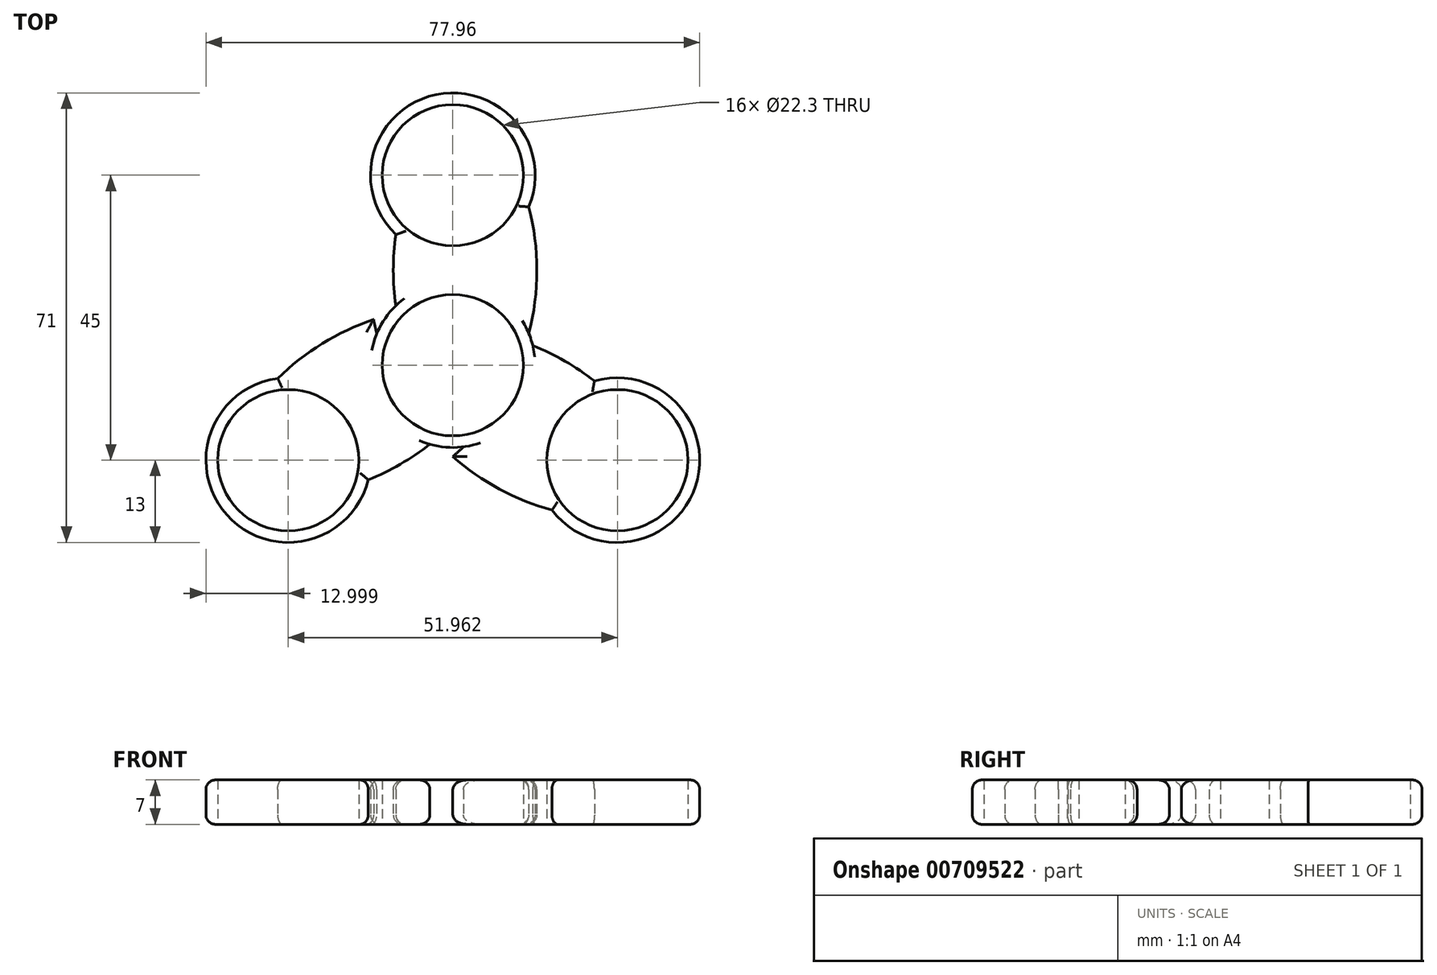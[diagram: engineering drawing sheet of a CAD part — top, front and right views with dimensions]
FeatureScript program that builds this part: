
annotation { "Feature Type Name" : "Feature", "Feature Type Description" : "" }
export const myFeature = defineFeature(function(context is Context, id is Id, definition is map)
    precondition{}
    {
        {
            var Q0;
            Q0=qCreatedBy(makeId("Top.planeOp"),FACE);
            var sketch = newSketch(context, id + "F0", { "sketchPlane" : qUnion([Q0])});
            skCircle(sketch, "E0", {"center": v(0, 0) * mm, "radius": 11.15 * mm});
            skCircle(sketch, "E1", {"center": v(0, 0) * mm, "radius": 13 * mm});
            skCircle(sketch, "E2", {"center": v(0, 30) * mm, "radius": 11.15 * mm});
            skCircle(sketch, "E3", {"center": v(0, 30) * mm, "radius": 13 * mm});
            skArc(sketch, "E4", {"start": v(12, 5) * mm, "mid": v(13.27, 15) * mm, "end": v(12, 25) * mm});
            skArc(sketch, "E5", {"start": v(9, 9.38) * mm, "mid": v(9.4, 15) * mm, "end": v(9, 20.62) * mm});
            skArc(sketch, "E6.MirrorCS", {"start": v(-9, 9.38) * mm, "mid": v(-9.4, 15) * mm, "end": v(-9, 20.62) * mm});
            skArc(sketch, "E7.MirrorCS", {"start": v(-12, 5) * mm, "mid": v(-13.27, 15) * mm, "end": v(-12, 25) * mm});
            skCircle(sketch, "E8.1.0", {"center": v(-25.98, -15) * mm, "radius": 13 * mm});
            skCircle(sketch, "E8.1.1", {"center": v(-25.98, -15) * mm, "radius": 11.15 * mm});
            skArc(sketch, "E8.1.2", {"start": v(1.67, -12.9) * mm, "mid": v(-6.36, -19) * mm, "end": v(-15.65, -22.9) * mm});
            skArc(sketch, "E8.1.5", {"start": v(-3.62, -12.48) * mm, "mid": v(-8.3, -15.64) * mm, "end": v(-13.36, -18.1) * mm});
            skArc(sketch, "E8.1.6", {"start": v(-10.33, 7.9) * mm, "mid": v(-19.63, 4) * mm, "end": v(-27.65, -2.1) * mm});
            skArc(sketch, "E8.1.7", {"start": v(-12.62, 3.1) * mm, "mid": v(-17.69, 0.64) * mm, "end": v(-22.36, -2.52) * mm});
            skCircle(sketch, "E8.2.0", {"center": v(25.98, -15) * mm, "radius": 13 * mm});
            skCircle(sketch, "E8.2.1", {"center": v(25.98, -15) * mm, "radius": 11.15 * mm});
            skArc(sketch, "E8.2.2", {"start": v(10.33, 7.9) * mm, "mid": v(19.63, 4) * mm, "end": v(27.65, -2.1) * mm});
            skArc(sketch, "E8.2.5", {"start": v(12.62, 3.1) * mm, "mid": v(17.69, 0.64) * mm, "end": v(22.36, -2.52) * mm});
            skArc(sketch, "E8.2.6", {"start": v(-1.67, -12.9) * mm, "mid": v(6.36, -19) * mm, "end": v(15.65, -22.9) * mm});
            skArc(sketch, "E8.2.7", {"start": v(3.62, -12.48) * mm, "mid": v(8.3, -15.64) * mm, "end": v(13.36, -18.1) * mm});
            skSolve(sketch);
        }
        {
            var Q0;
            Q0=makeQuery(id+"F0.imprint","IMPRINT",FACE,{"disambiguationData":[TD([[makeQuery(id+"F0.imprint","IMPRINT",EDGE,{"derivedFrom":sQuery(id+"F0.wireOp",EDGE,"E8.1.1")}),-1.0]])]});
            var Q1;
            {var subQ0=sQuery(id+"F0.wireOp",EDGE,"E8.1.7");Q1=makeQuery(id+"F0.imprint","IMPRINT",FACE,{"disambiguationData":[TD([[makeQuery(id+"F0.imprint","IMPRINT",EDGE,{"derivedFrom":subQ0}),-1.0]])]});}
            var Q2;
            {var subQ1=sQuery(id+"F0.wireOp",EDGE,"E8.1.5");Q2=makeQuery(id+"F0.imprint","IMPRINT",FACE,{"disambiguationData":[TD([[makeQuery(id+"F0.imprint","IMPRINT",EDGE,{"derivedFrom":subQ1}),1.0]])]});}
            var Q3;
            Q3=makeQuery(id+"F0.imprint","IMPRINT",FACE,{"disambiguationData":[TD([[makeQuery(id+"F0.imprint","IMPRINT",EDGE,{"derivedFrom":sQuery(id+"F0.wireOp",EDGE,"E0")}),-1.0]])]});
            var Q4;
            {var subQ5=sQuery(id+"F0.wireOp",EDGE,"E6.MirrorCS");Q4=makeQuery(id+"F0.imprint","IMPRINT",FACE,{"disambiguationData":[TD([[makeQuery(id+"F0.imprint","IMPRINT",EDGE,{"derivedFrom":subQ5}),1.0]])]});}
            var Q5;
            {var subQ5=sQuery(id+"F0.wireOp",EDGE,"E5");Q5=makeQuery(id+"F0.imprint","IMPRINT",FACE,{"disambiguationData":[TD([[makeQuery(id+"F0.imprint","IMPRINT",EDGE,{"derivedFrom":subQ5}),-1.0]])]});}
            var Q6;
            Q6=makeQuery(id+"F0.imprint","IMPRINT",FACE,{"disambiguationData":[TD([[makeQuery(id+"F0.imprint","IMPRINT",EDGE,{"derivedFrom":sQuery(id+"F0.wireOp",EDGE,"E2")}),-1.0]])]});
            var Q7;
            {var subQ3=sQuery(id+"F0.wireOp",EDGE,"E8.2.5");Q7=makeQuery(id+"F0.imprint","IMPRINT",FACE,{"disambiguationData":[TD([[makeQuery(id+"F0.imprint","IMPRINT",EDGE,{"derivedFrom":subQ3}),1.0]])]});}
            var Q8;
            Q8=makeQuery(id+"F0.imprint","IMPRINT",FACE,{"disambiguationData":[TD([[makeQuery(id+"F0.imprint","IMPRINT",EDGE,{"derivedFrom":sQuery(id+"F0.wireOp",EDGE,"E8.2.1")}),-1.0]])]});
            var Q9;
            {var subQ0=sQuery(id+"F0.wireOp",EDGE,"E1");var subQ1=sQuery(id+"F0.wireOp",EDGE,"E8.1.2");var subQ2=makeQuery(id+"F0.imprint","INTERSECT",VERTEX,{"derivedFrom":[subQ1,subQ0]});Q9=makeQuery(id+"F0.imprint","IMPRINT",FACE,{"disambiguationData":[TD([[makeQuery(id+"F0.imprint","IMPRINT",EDGE,{"disambiguationData":[TD([[subQ2,-1.0]])],"derivedFrom":subQ1}),-1.0]])]});}
            var Q10;
            {var subQ0=sQuery(id+"F0.wireOp",EDGE,"E1");var subQ1=sQuery(id+"F0.wireOp",EDGE,"E4");var subQ2=makeQuery(id+"F0.imprint","INTERSECT",VERTEX,{"derivedFrom":[subQ1,subQ0]});Q10=makeQuery(id+"F0.imprint","IMPRINT",FACE,{"disambiguationData":[TD([[makeQuery(id+"F0.imprint","IMPRINT",EDGE,{"disambiguationData":[TD([[subQ2,-1.0]])],"derivedFrom":subQ1}),1.0]])]});}
            var Q11;
            {var subQ0=sQuery(id+"F0.wireOp",EDGE,"E1");var subQ1=sQuery(id+"F0.wireOp",EDGE,"E7.MirrorCS");var subQ2=makeQuery(id+"F0.imprint","INTERSECT",VERTEX,{"derivedFrom":[subQ1,subQ0]});Q11=makeQuery(id+"F0.imprint","IMPRINT",FACE,{"disambiguationData":[TD([[makeQuery(id+"F0.imprint","IMPRINT",EDGE,{"disambiguationData":[TD([[subQ2,-1.0]])],"derivedFrom":subQ1}),-1.0]])]});}
            var Q12;
            {var subQ5=sQuery(id+"F0.wireOp",EDGE,"E8.2.7");Q12=makeQuery(id+"F0.imprint","IMPRINT",FACE,{"disambiguationData":[TD([[makeQuery(id+"F0.imprint","IMPRINT",EDGE,{"derivedFrom":subQ5}),-1.0]])]});}
            extrude(context, id + "F1", {"entities" : qUnion([Q0, Q1, Q2, Q3, Q4, Q5, Q6, Q7, Q8, Q9, Q10, Q11, Q12]), "depth" : 7 * mm, "offsetDistance" : 25 * mm});
        }
        {
            var Q0;
            Q0=makeQuery(id+"F1.opExtrude","CAP_EDGE",EDGE,{"disambiguationData":[OSD([sQuery(id+"F0.wireOp",EDGE,"E8.1.6")])],"isStart":false});
            var Q1;
            Q1=makeQuery(id+"F1.opExtrude","CAP_EDGE",EDGE,{"disambiguationData":[OSD([sQuery(id+"F0.wireOp",EDGE,"E8.1.7")])],"isStart":false});
            var Q2;
            Q2=makeQuery(id+"F1.opExtrude","CAP_EDGE",EDGE,{"disambiguationData":[OSD([sQuery(id+"F0.wireOp",EDGE,"E8.1.5")])],"isStart":false});
            var Q3;
            {var subQ0=sQuery(id+"F0.wireOp",EDGE,"E8.1.0");Q3=makeQuery(id+"F1.opExtrude","CAP_EDGE",EDGE,{"disambiguationData":[OSD([subQ0]),TDD([makeQuery(id+"F0.imprint","IMPRINT",EDGE,{"disambiguationData":[TD([[makeQuery(id+"F0.imprint","INTERSECT",VERTEX,{"derivedFrom":[subQ0,sQuery(id+"F0.wireOp",EDGE,"E8.1.5")]}),-1.0]])],"derivedFrom":subQ0})])],"isStart":false});}
            var Q4;
            {var subQ0=sQuery(id+"F0.wireOp",EDGE,"E8.1.0");Q4=makeQuery(id+"F1.opExtrude","CAP_EDGE",EDGE,{"disambiguationData":[OSD([subQ0]),TDD([makeQuery(id+"F0.imprint","IMPRINT",EDGE,{"disambiguationData":[TD([[makeQuery(id+"F0.imprint","INTERSECT",VERTEX,{"derivedFrom":[subQ0,sQuery(id+"F0.wireOp",EDGE,"E8.1.2")]}),1.0]])],"derivedFrom":subQ0})])],"isStart":false});}
            var Q5;
            Q5=makeQuery(id+"F1.opExtrude","CAP_EDGE",EDGE,{"disambiguationData":[OSD([sQuery(id+"F0.wireOp",EDGE,"E8.1.2")])],"isStart":false});
            var Q6;
            Q6=makeQuery(id+"F1.opExtrude","CAP_EDGE",EDGE,{"disambiguationData":[OSD([sQuery(id+"F0.wireOp",EDGE,"E8.1.2")])],"isStart":true});
            var Q7;
            {var subQ0=sQuery(id+"F0.wireOp",EDGE,"E8.1.0");Q7=makeQuery(id+"F1.opExtrude","CAP_EDGE",EDGE,{"disambiguationData":[OSD([subQ0]),TDD([makeQuery(id+"F0.imprint","IMPRINT",EDGE,{"disambiguationData":[TD([[makeQuery(id+"F0.imprint","INTERSECT",VERTEX,{"derivedFrom":[subQ0,sQuery(id+"F0.wireOp",EDGE,"E8.1.2")]}),1.0]])],"derivedFrom":subQ0})])],"isStart":true});}
            var Q8;
            {var subQ0=sQuery(id+"F0.wireOp",EDGE,"E8.1.0");Q8=makeQuery(id+"F1.opExtrude","CAP_EDGE",EDGE,{"disambiguationData":[OSD([subQ0]),TDD([makeQuery(id+"F0.imprint","IMPRINT",EDGE,{"disambiguationData":[TD([[makeQuery(id+"F0.imprint","INTERSECT",VERTEX,{"derivedFrom":[subQ0,sQuery(id+"F0.wireOp",EDGE,"E8.1.5")]}),-1.0]])],"derivedFrom":subQ0})])],"isStart":true});}
            var Q9;
            {var subQ0=sQuery(id+"F0.wireOp",EDGE,"E1");Q9=makeQuery(id+"F1.opExtrude","CAP_EDGE",EDGE,{"disambiguationData":[OSD([subQ0]),TDD([makeQuery(id+"F0.imprint","IMPRINT",EDGE,{"disambiguationData":[TD([[makeQuery(id+"F0.imprint","INTERSECT",VERTEX,{"derivedFrom":[sQuery(id+"F0.wireOp",EDGE,"E8.1.5"),subQ0]}),1.0]])],"derivedFrom":subQ0})])],"isStart":false});}
            var Q10;
            Q10=makeQuery(id+"F1.opExtrude","CAP_EDGE",EDGE,{"disambiguationData":[OSD([sQuery(id+"F0.wireOp",EDGE,"E7.MirrorCS")])],"isStart":false});
            var Q11;
            Q11=makeQuery(id+"F1.opExtrude","CAP_EDGE",EDGE,{"disambiguationData":[OSD([sQuery(id+"F0.wireOp",EDGE,"E6.MirrorCS")])],"isStart":false});
            var Q12;
            {var subQ0=sQuery(id+"F0.wireOp",EDGE,"E1");Q12=makeQuery(id+"F1.opExtrude","CAP_EDGE",EDGE,{"disambiguationData":[OSD([subQ0]),TDD([makeQuery(id+"F0.imprint","IMPRINT",EDGE,{"disambiguationData":[TD([[makeQuery(id+"F0.imprint","INTERSECT",VERTEX,{"derivedFrom":[sQuery(id+"F0.wireOp",EDGE,"E5"),subQ0]}),-1.0]])],"derivedFrom":subQ0})])],"isStart":false});}
            var Q13;
            {var subQ0=sQuery(id+"F0.wireOp",EDGE,"E1");Q13=makeQuery(id+"F1.opExtrude","CAP_EDGE",EDGE,{"disambiguationData":[OSD([subQ0]),TDD([makeQuery(id+"F0.imprint","IMPRINT",EDGE,{"disambiguationData":[TD([[makeQuery(id+"F0.imprint","INTERSECT",VERTEX,{"derivedFrom":[subQ0,sQuery(id+"F0.wireOp",EDGE,"E8.2.5")]}),1.0]])],"derivedFrom":subQ0})])],"isStart":false});}
            var Q14;
            Q14=makeQuery(id+"F1.opExtrude","CAP_EDGE",EDGE,{"disambiguationData":[OSD([sQuery(id+"F0.wireOp",EDGE,"E5")])],"isStart":false});
            var Q15;
            Q15=makeQuery(id+"F1.opExtrude","CAP_EDGE",EDGE,{"disambiguationData":[OSD([sQuery(id+"F0.wireOp",EDGE,"E4")])],"isStart":false});
            var Q16;
            Q16=makeQuery(id+"F1.opExtrude","CAP_EDGE",EDGE,{"disambiguationData":[OSD([sQuery(id+"F0.wireOp",EDGE,"E8.2.2")])],"isStart":false});
            var Q17;
            Q17=makeQuery(id+"F1.opExtrude","CAP_EDGE",EDGE,{"disambiguationData":[OSD([sQuery(id+"F0.wireOp",EDGE,"E8.2.5")])],"isStart":false});
            var Q18;
            Q18=makeQuery(id+"F1.opExtrude","CAP_EDGE",EDGE,{"disambiguationData":[OSD([sQuery(id+"F0.wireOp",EDGE,"E8.2.7")])],"isStart":false});
            var Q19;
            Q19=makeQuery(id+"F1.opExtrude","CAP_EDGE",EDGE,{"disambiguationData":[OSD([sQuery(id+"F0.wireOp",EDGE,"E8.2.6")])],"isStart":false});
            var Q20;
            {var subQ0=sQuery(id+"F0.wireOp",EDGE,"E8.2.0");Q20=makeQuery(id+"F1.opExtrude","CAP_EDGE",EDGE,{"disambiguationData":[OSD([subQ0]),TDD([makeQuery(id+"F0.imprint","IMPRINT",EDGE,{"disambiguationData":[TD([[makeQuery(id+"F0.imprint","INTERSECT",VERTEX,{"derivedFrom":[subQ0,sQuery(id+"F0.wireOp",EDGE,"E8.2.2")]}),1.0]])],"derivedFrom":subQ0})])],"isStart":false});}
            var Q21;
            {var subQ0=sQuery(id+"F0.wireOp",EDGE,"E8.2.0");Q21=makeQuery(id+"F1.opExtrude","CAP_EDGE",EDGE,{"disambiguationData":[OSD([subQ0]),TDD([makeQuery(id+"F0.imprint","IMPRINT",EDGE,{"disambiguationData":[TD([[makeQuery(id+"F0.imprint","INTERSECT",VERTEX,{"derivedFrom":[subQ0,sQuery(id+"F0.wireOp",EDGE,"E8.2.5")]}),-1.0]])],"derivedFrom":subQ0})])],"isStart":false});}
            var Q22;
            {var subQ0=sQuery(id+"F0.wireOp",EDGE,"E3");Q22=makeQuery(id+"F1.opExtrude","CAP_EDGE",EDGE,{"disambiguationData":[OSD([subQ0]),TDD([makeQuery(id+"F0.imprint","IMPRINT",EDGE,{"disambiguationData":[TD([[makeQuery(id+"F0.imprint","INTERSECT",VERTEX,{"derivedFrom":[subQ0,sQuery(id+"F0.wireOp",EDGE,"E5")]}),1.0]])],"derivedFrom":subQ0})])],"isStart":false});}
            var Q23;
            {var subQ0=sQuery(id+"F0.wireOp",EDGE,"E3");Q23=makeQuery(id+"F1.opExtrude","CAP_EDGE",EDGE,{"disambiguationData":[OSD([subQ0]),TDD([makeQuery(id+"F0.imprint","IMPRINT",EDGE,{"disambiguationData":[TD([[makeQuery(id+"F0.imprint","INTERSECT",VERTEX,{"derivedFrom":[subQ0,sQuery(id+"F0.wireOp",EDGE,"E4")]}),-1.0]])],"derivedFrom":subQ0})])],"isStart":false});}
            var Q24;
            {var subQ0=sQuery(id+"F0.wireOp",EDGE,"E8.2.0");Q24=makeQuery(id+"F1.opExtrude","CAP_EDGE",EDGE,{"disambiguationData":[OSD([subQ0]),TDD([makeQuery(id+"F0.imprint","IMPRINT",EDGE,{"disambiguationData":[TD([[makeQuery(id+"F0.imprint","INTERSECT",VERTEX,{"derivedFrom":[subQ0,sQuery(id+"F0.wireOp",EDGE,"E8.2.2")]}),1.0]])],"derivedFrom":subQ0})])],"isStart":true});}
            var Q25;
            {var subQ0=sQuery(id+"F0.wireOp",EDGE,"E8.2.0");Q25=makeQuery(id+"F1.opExtrude","CAP_EDGE",EDGE,{"disambiguationData":[OSD([subQ0]),TDD([makeQuery(id+"F0.imprint","IMPRINT",EDGE,{"disambiguationData":[TD([[makeQuery(id+"F0.imprint","INTERSECT",VERTEX,{"derivedFrom":[subQ0,sQuery(id+"F0.wireOp",EDGE,"E8.2.5")]}),-1.0]])],"derivedFrom":subQ0})])],"isStart":true});}
            var Q26;
            {var subQ0=sQuery(id+"F0.wireOp",EDGE,"E1");Q26=makeQuery(id+"F1.opExtrude","CAP_EDGE",EDGE,{"disambiguationData":[OSD([subQ0]),TDD([makeQuery(id+"F0.imprint","IMPRINT",EDGE,{"disambiguationData":[TD([[makeQuery(id+"F0.imprint","INTERSECT",VERTEX,{"derivedFrom":[subQ0,sQuery(id+"F0.wireOp",EDGE,"E8.2.5")]}),1.0]])],"derivedFrom":subQ0})])],"isStart":true});}
            var Q27;
            {var subQ0=sQuery(id+"F0.wireOp",EDGE,"E1");Q27=makeQuery(id+"F1.opExtrude","CAP_EDGE",EDGE,{"disambiguationData":[OSD([subQ0]),TDD([makeQuery(id+"F0.imprint","IMPRINT",EDGE,{"disambiguationData":[TD([[makeQuery(id+"F0.imprint","INTERSECT",VERTEX,{"derivedFrom":[sQuery(id+"F0.wireOp",EDGE,"E5"),subQ0]}),-1.0]])],"derivedFrom":subQ0})])],"isStart":true});}
            var Q28;
            {var subQ0=sQuery(id+"F0.wireOp",EDGE,"E1");Q28=makeQuery(id+"F1.opExtrude","CAP_EDGE",EDGE,{"disambiguationData":[OSD([subQ0]),TDD([makeQuery(id+"F0.imprint","IMPRINT",EDGE,{"disambiguationData":[TD([[makeQuery(id+"F0.imprint","INTERSECT",VERTEX,{"derivedFrom":[sQuery(id+"F0.wireOp",EDGE,"E8.1.5"),subQ0]}),1.0]])],"derivedFrom":subQ0})])],"isStart":true});}
            var Q29;
            {var subQ0=sQuery(id+"F0.wireOp",EDGE,"E3");Q29=makeQuery(id+"F1.opExtrude","CAP_EDGE",EDGE,{"disambiguationData":[OSD([subQ0]),TDD([makeQuery(id+"F0.imprint","IMPRINT",EDGE,{"disambiguationData":[TD([[makeQuery(id+"F0.imprint","INTERSECT",VERTEX,{"derivedFrom":[subQ0,sQuery(id+"F0.wireOp",EDGE,"E5")]}),1.0]])],"derivedFrom":subQ0})])],"isStart":true});}
            var Q30;
            {var subQ0=sQuery(id+"F0.wireOp",EDGE,"E3");Q30=makeQuery(id+"F1.opExtrude","CAP_EDGE",EDGE,{"disambiguationData":[OSD([subQ0]),TDD([makeQuery(id+"F0.imprint","IMPRINT",EDGE,{"disambiguationData":[TD([[makeQuery(id+"F0.imprint","INTERSECT",VERTEX,{"derivedFrom":[subQ0,sQuery(id+"F0.wireOp",EDGE,"E4")]}),-1.0]])],"derivedFrom":subQ0})])],"isStart":true});}
            var Q31;
            Q31=makeQuery(id+"F1.opExtrude","CAP_EDGE",EDGE,{"disambiguationData":[OSD([sQuery(id+"F0.wireOp",EDGE,"E8.2.5")])],"isStart":true});
            var Q32;
            Q32=makeQuery(id+"F1.opExtrude","CAP_EDGE",EDGE,{"disambiguationData":[OSD([sQuery(id+"F0.wireOp",EDGE,"E8.2.7")])],"isStart":true});
            var Q33;
            Q33=makeQuery(id+"F1.opExtrude","CAP_EDGE",EDGE,{"disambiguationData":[OSD([sQuery(id+"F0.wireOp",EDGE,"E6.MirrorCS")])],"isStart":true});
            var Q34;
            Q34=makeQuery(id+"F1.opExtrude","CAP_EDGE",EDGE,{"disambiguationData":[OSD([sQuery(id+"F0.wireOp",EDGE,"E5")])],"isStart":true});
            var Q35;
            Q35=makeQuery(id+"F1.opExtrude","CAP_EDGE",EDGE,{"disambiguationData":[OSD([sQuery(id+"F0.wireOp",EDGE,"E8.1.7")])],"isStart":true});
            var Q36;
            Q36=makeQuery(id+"F1.opExtrude","CAP_EDGE",EDGE,{"disambiguationData":[OSD([sQuery(id+"F0.wireOp",EDGE,"E8.1.6")])],"isStart":true});
            var Q37;
            Q37=makeQuery(id+"F1.opExtrude","CAP_EDGE",EDGE,{"disambiguationData":[OSD([sQuery(id+"F0.wireOp",EDGE,"E8.1.5")])],"isStart":true});
            var Q38;
            Q38=makeQuery(id+"F1.opExtrude","CAP_EDGE",EDGE,{"disambiguationData":[OSD([sQuery(id+"F0.wireOp",EDGE,"E8.2.2")])],"isStart":true});
            var Q39;
            Q39=makeQuery(id+"F1.opExtrude","CAP_EDGE",EDGE,{"disambiguationData":[OSD([sQuery(id+"F0.wireOp",EDGE,"E7.MirrorCS")])],"isStart":true});
            var Q40;
            Q40=makeQuery(id+"F1.opExtrude","CAP_EDGE",EDGE,{"disambiguationData":[OSD([sQuery(id+"F0.wireOp",EDGE,"E4")])],"isStart":true});
            var Q41;
            Q41=makeQuery(id+"F1.opExtrude","CAP_EDGE",EDGE,{"disambiguationData":[OSD([sQuery(id+"F0.wireOp",EDGE,"E8.2.6")])],"isStart":true});
            fillet(context, id + "F2", {"entities" : qUnion([Q0, Q1, Q2, Q3, Q4, Q5, Q6, Q7, Q8, Q9, Q10, Q11, Q12, Q13, Q14, Q15, Q16, Q17, Q18, Q19, Q20, Q21, Q22, Q23, Q24, Q25, Q26, Q27, Q28, Q29, Q30, Q31, Q32, Q33, Q34, Q35, Q36, Q37, Q38, Q39, Q40, Q41]), "radius" : 1.5 * mm, "tangentPropagation" : true, "allowEdgeOverflow" : false});
        }
    });
